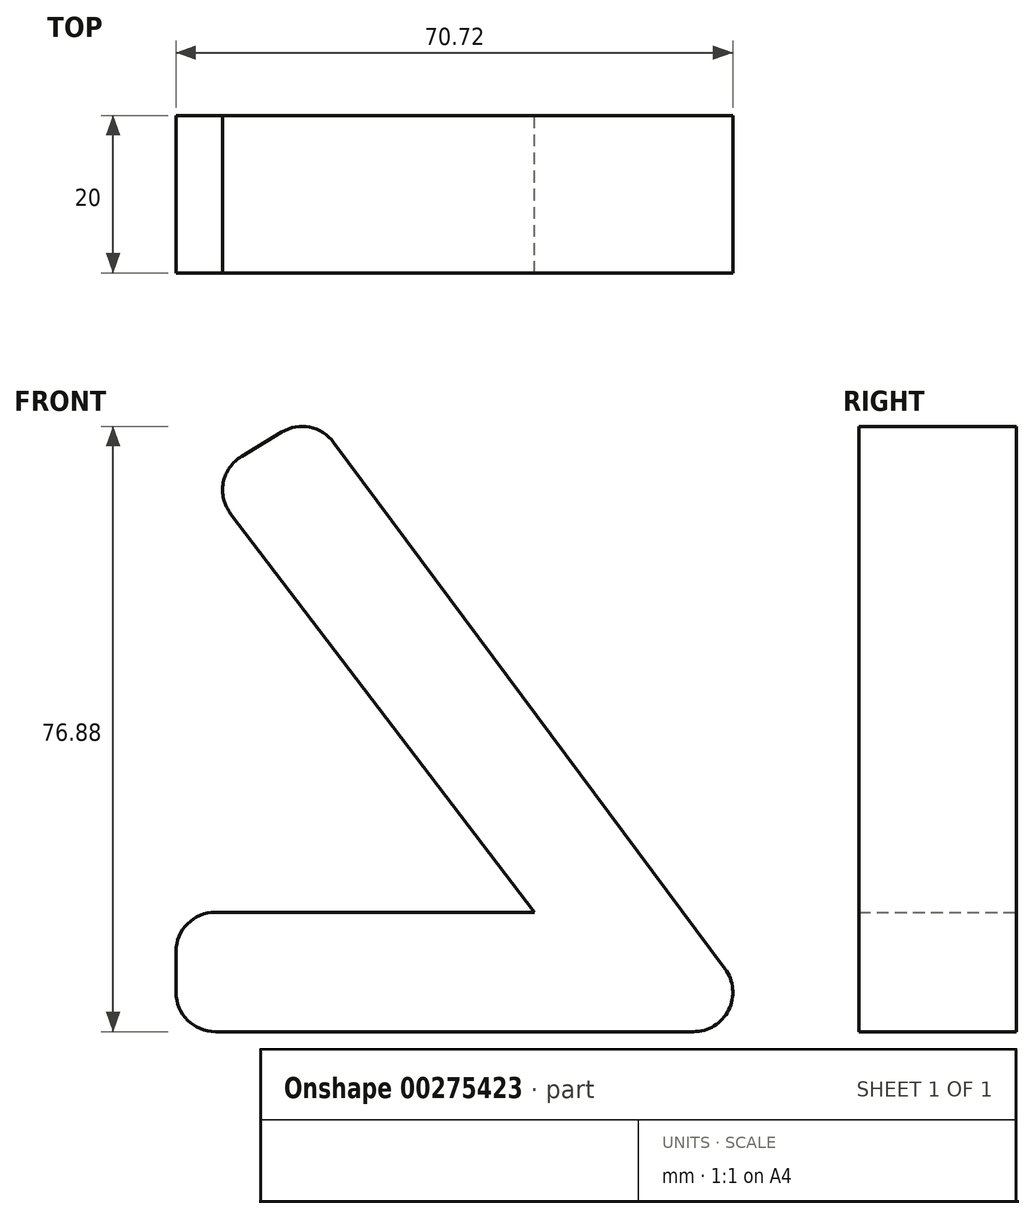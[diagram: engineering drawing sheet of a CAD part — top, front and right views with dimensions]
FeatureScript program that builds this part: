
annotation { "Feature Type Name" : "Feature", "Feature Type Description" : "" }
export const myFeature = defineFeature(function(context is Context, id is Id, definition is map)
    precondition{}
    {
        {
            var Q0;
            Q0=qCreatedBy(makeId("Front.planeOp"),FACE);
            var sketch = newSketch(context, id + "F0", { "sketchPlane" : qUnion([Q0])});
            skLineSegment(sketch, "E0", {"start": v(-14.13, 41.19) * mm, "end": v(35.58, -25.7) * mm});
            skLineSegment(sketch, "E1", {"start": v(31.56, -33.68) * mm, "end": v(-29.16, -33.68) * mm});
            skLineSegment(sketch, "E2", {"start": v(-34.16, -28.68) * mm, "end": v(-34.16, -23.5) * mm});
            skLineSegment(sketch, "E3", {"start": v(-29.16, -18.5) * mm, "end": v(11.39, -18.5) * mm});
            skLineSegment(sketch, "E4", {"start": v(11.39, -18.5) * mm, "end": v(-27.22, 32.1) * mm});
            skLineSegment(sketch, "E5", {"start": v(-25.82, 39.4) * mm, "end": v(-20.73, 42.48) * mm});
            skPoint(sketch, "E6.visualSharp", {"position": v(41.5, -33.68) * mm});
            skArc(sketch, "E6.filletArc", {"start": v(31.56, -33.68) * mm, "mid": v(36.03, -30.93) * mm, "end": v(35.58, -25.7) * mm});
            skPoint(sketch, "E7.visualSharp", {"position": v(-34.16, -33.68) * mm});
            skArc(sketch, "E7.filletArc", {"start": v(-34.16, -28.68) * mm, "mid": v(-32.7, -32.22) * mm, "end": v(-29.16, -33.68) * mm});
            skPoint(sketch, "E8.visualSharp", {"position": v(-34.16, -18.5) * mm});
            skArc(sketch, "E8.filletArc", {"start": v(-29.16, -18.5) * mm, "mid": v(-32.7, -19.97) * mm, "end": v(-34.16, -23.5) * mm});
            skPoint(sketch, "E9.visualSharp", {"position": v(-16.84, 44.83) * mm});
            skArc(sketch, "E9.filletArc", {"start": v(-14.13, 41.19) * mm, "mid": v(-17.18, 43.1) * mm, "end": v(-20.73, 42.48) * mm});
            skPoint(sketch, "E10.visualSharp", {"position": v(-30.6, 36.53) * mm});
            skArc(sketch, "E10.filletArc", {"start": v(-25.82, 39.4) * mm, "mid": v(-28.15, 36.06) * mm, "end": v(-27.22, 32.1) * mm});
            skSolve(sketch);
        }
        {
            var Q0;
            Q0 = qSketchRegion(id + "F0", true);
            extrude(context, id + "F1", {"entities" : qUnion([Q0]), "depth" : 20 * mm});
        }
    });
